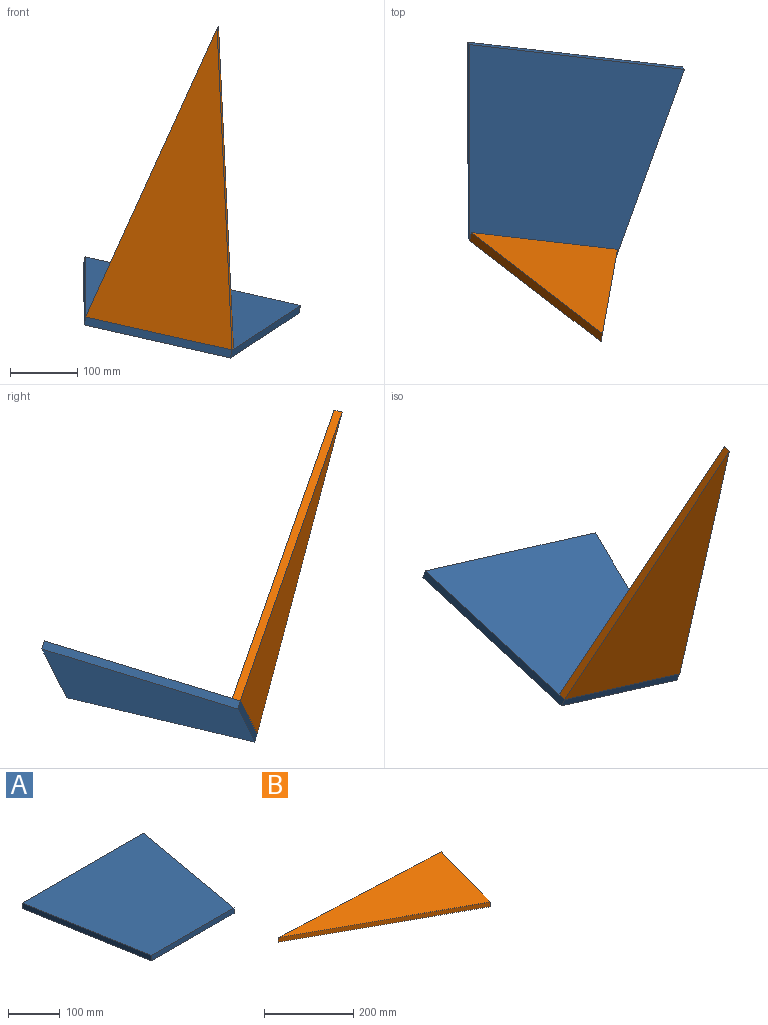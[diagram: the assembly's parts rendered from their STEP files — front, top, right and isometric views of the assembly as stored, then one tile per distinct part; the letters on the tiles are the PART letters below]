
ASSEMBLY  parts=2 mates=1
PART A: 6 faces, bbox 330.2x300.2x12.7 mm
  f0: plane 224.34x12.7mm, normal (0,-1,0), area 2849.2mm2, adj f1,f3,f4,f5
  f1: plane 300.17x52.93mm, normal (0.98,-0.17,0), area 3871mm2, adj f0,f2,f4,f5
  f2: plane 330.2x12.7mm, normal (0,1,0), area 4193.5mm2, adj f1,f3,f4,f5
  f3: plane 300.17x52.93mm, normal (-0.98,-0.17,0), area 3871mm2, adj f0,f2,f4,f5
  f4: plane 330.2x300.17mm, normal (0,0,-1), area 83228.6mm2, adj f0,f1,f2,f3
  f5: plane 330.2x300.17mm, normal (0,0,1), area 83228.6mm2, adj f0,f1,f2,f3
PART B: 5 faces, bbox 494.8x238.4x12.7 mm
  f0: plane 434.14x238.41mm, normal (-0.48,-0.88,0), area 6290.3mm2, adj f1,f2,f3,f4
  f1: plane 215.98x60.65mm, normal (0.96,-0.27,0), area 2849mm2, adj f0,f2,f3,f4
  f2: plane 494.79x22.43mm, normal (0.05,1,0), area 6290.3mm2, adj f0,f1,f3,f4
  f3: plane 494.79x238.41mm, normal (0,0,1), area 54112.7mm2, adj f0,f1,f2
  f4: plane 494.79x238.41mm, normal (0,0,-1), area 54112.7mm2, adj f0,f1,f2
PLACE A rot(axis=(0.75,0.54,-0.38),21.4deg) t=(72.07,190.21,104.27)mm
PLACE B rot(axis=(-0.3,0.62,0.73),125deg) t=(270.54,-164.63,271.19)mm
MATE fastened B.f1 <-> A.f5  axis (-0.18,0.29,-0.94) through (81.75,-64.26,24.64)mm
